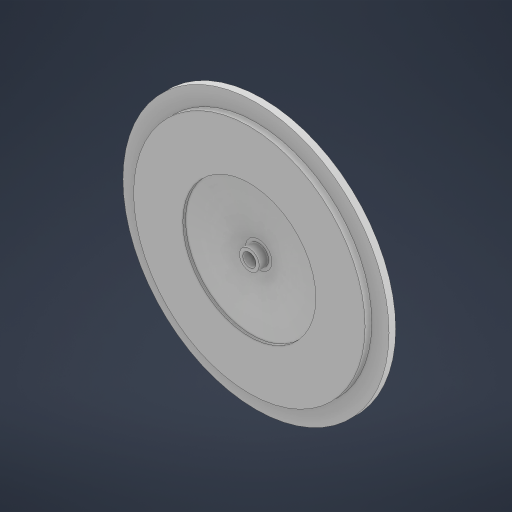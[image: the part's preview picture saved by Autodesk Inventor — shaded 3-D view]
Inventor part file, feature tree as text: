
AUTODESK INVENTOR PART (.ipt)
format: ipt  version: 2023 (Build 270158000, 158)  size: 216,064 bytes
history: native  units: mm
features: extrude x4, sketch x4, chamfer x1
ambient origin geometry x8: Origin, YZ Plane, XZ Plane, XY Plane, X Axis, Y Axis, Z Axis, Center Point
bodies: Solid1 (feature_tree)
feature tree (9):
  extrude  "Extrusion1"  Depth=5.0mm TaperAngle=0.0deg
  extrude  "Extrusion2"  Depth=5.0mm TaperAngle=0.0deg
  extrude  "Extrusion3"  Depth=10.0mm TaperAngle=0.0deg
  extrude  "Extrusion4"  Depth=100.0mm
  chamfer  "Chamfer1"  Distance=7.0mm
  sketch  "Sketch1"  dims[d0=200.0mm d1=5.0mm d2=0.0mm]
  sketch  "Sketch2"  dims[d3=174.0mm d4=5.0mm d5=0.0mm]
  sketch  "Sketch3"  dims[d6=10.0mm d7=10.0mm d8=0.0mm]
  sketch  "Sketch4"  dims[d9=15.0mm d10=100.0mm d11=7.0mm d12=0.0mm d13=5.0mm d14=40.0mm d15=45.0deg]
